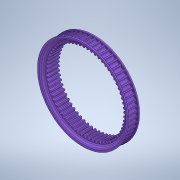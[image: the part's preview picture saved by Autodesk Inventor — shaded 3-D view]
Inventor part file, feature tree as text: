
AUTODESK INVENTOR PART (.ipt)
format: ipt  version: 2020 (Build 240168000, 168)  size: 1,907,712 bytes
history: native  units: mm (DEFAULTED — no unit token found)
features: sketch x5, extrude x4, plane x4, other x3, revolve x1, chamfer x1, mirror x1, fillet x1
ambient origin geometry x8: Origin, YZ Plane, XZ Plane, XY Plane, X Axis, Y Axis, Z Axis, Center Point
bodies: Solid1 (feature_tree)
feature tree (20):
  extrude  "Extrusion1"  Depth=15.875mm TaperAngle=0.0deg
  plane  "Work Plane1"
  plane  "Work Plane2"
  plane  "Work Plane3"
  other  "Spur Gear"
  sketch  "Sketch3"  dims[d6=0.0mm d7=0.490874mm d9=0.0mm]
  extrude  "Extrusion2"  Depth=76.2mm TaperAngle=0.0deg
  extrude  "Extrusion3"  TaperAngle=0.0deg  [1 undecoded]
  revolve  "Revolution4"  [1 undecoded]
  plane  "Work Plane6"
  extrude  "Extrusion8"  Depth=1.5875mm
  chamfer  "Chamfer2"  Distance=90.19mm
  mirror  "Mirror3"
  fillet  "Fillet3"  Radius=1.047198mm
  sketch  "Sketch1"  dims[d0=92.9005mm d1=15.875mm d2=0.0mm]
  sketch  "Sketch2"  dims[d3=81.28mm d4=76.2mm d5=0.0mm]
  other  "Srf1"
  sketch  "Sketch10"  dims[d14=0.0mm d15=30.48mm d16=0.0mm]
  sketch  "Sketch11"  dims[d17=0.0mm d18=0.0mm d19=30.48mm d20=94.35mm d21=90.19mm d23=1.047198mm d24=3.05mm d26=600.0mm d28=360.0deg d30=25.4mm d31=0.0mm d32=25.4mm d33=0.0mm d34=0.01mm d35=0.01mm d52=0.9mm d67=15.875mm d68=3.175mm d69=3.175mm d70=12.7mm d71=60.0deg d73=90.0deg d77=95.25mm d78=1.5875mm d79=0.0mm d80=0.396875mm d81=3.175mm d82=45.0deg d83=0.254mm d84=43.815mm d85=1.5875mm d86=30.0deg d87=0.872665mm d88=0.872665mm]
  other  "Pitch Diameter"
note: 2 required parameter values undecoded (feature->parameter linkage not recoverable at this tier; creation-order binding heuristic only, values carry confidence <= 0.55)